# Revit family: Sanitary_Shower-trays_DURAVIT-AG_D-Code-Shower-tray-1400x700-mm-720095
name_source: partatom
category: Plumbing Fixtures
units: mm (PartAtom-declared; Revit-internal decimal feet)

## family parameters
Cut with Voids When Loaded = Yes
Host = Face
Maintain Annotation Orientation = No
OmniClass Number = 23.31.17.15
OmniClass Title = Shower Enclosure Bases
Part Type = Normal
Room Calculation Point = No
Round Connector Dimension = Use Diameter
Shared = No

## types (2) — shared parameters
Depth = 700 mm  [stored 2.29659 ft]
Diameter = 90 mm  [stored 0.295276 ft]
Height = 85 mm  [stored 0.278871 ft]
Installation instructions = https://duravit-public-assets.s3.eu-central-1.amazonaws.com
Manufacturer = Duravit
Material 1 = Duravit - Plastic - 00 - White Alpin
Material 2 = Duravit - Metal - 10 - Chrome
Model = D-Code Shower tray 1400x700 mm - 720095
Product Documentation Link = https://pro.duravit.com
Product Page URL = https://pro.duravit.com
Product data url = https://bimobject.com
URL = http://pro.duravit.com
Version = 1
Weight = 20.50 kg
Width = 1400 mm  [stored 4.59318 ft]
zero-valued in all types: Default Elevation

## per-type parameters (varying)
| type | Description |
| 00 - White Alpin - 720095000000000 | Duravit D-Code Shower tray, Rectangular, White, Material: Sanitary acrylic, Waste outlet position: Corner, Height: 85 mm - 720095000000000 |
| 00 - White Alpin - 720095000000001 | Duravit D-Code Shower tray, Rectangular, White, Material: Sanitary acrylic, Waste outlet position: Corner, Height: 85 mm - 720095000000001 |

note: [stored X ft] marks values corroborated as IEEE doubles in the binary element streams (Revit-internal decimal feet)

## geometry (parser evidence)
native form markers: Sweep x2
no freeform markers — native parametric forms only
